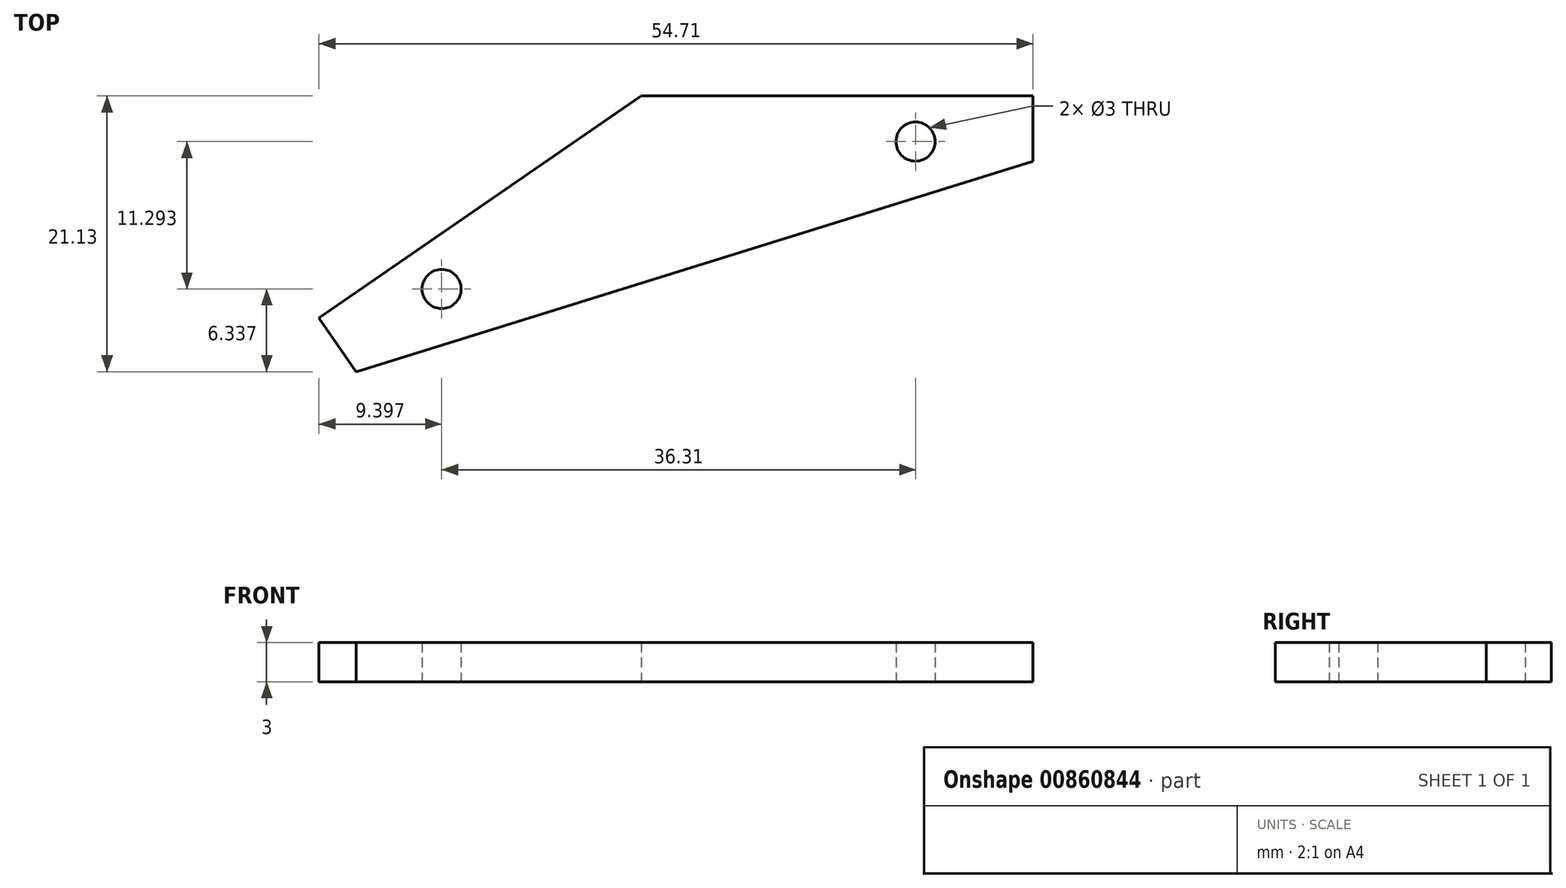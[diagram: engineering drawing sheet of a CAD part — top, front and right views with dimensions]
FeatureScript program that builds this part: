
annotation { "Feature Type Name" : "Feature", "Feature Type Description" : "" }
export const myFeature = defineFeature(function(context is Context, id is Id, definition is map)
    precondition{}
    {
        {
            var Q0;
            Q0=qCreatedBy(makeId("Top.planeOp"),FACE);
            var sketch = newSketch(context, id + "F0", { "sketchPlane" : qUnion([Q0])});
            skLineSegment(sketch, "E0", {"start": v(-50.25, 0) * mm, "end": v(-20.25, 0) * mm});
            skLineSegment(sketch, "E1", {"start": v(-50.25, 0) * mm, "end": v(-74.96, -17.02) * mm});
            skLineSegment(sketch, "E2", {"start": v(-74.96, -17.02) * mm, "end": v(-72.12, -21.13) * mm});
            skLineSegment(sketch, "E3", {"start": v(-72.12, -21.13) * mm, "end": v(-20.25, -5) * mm});
            skLineSegment(sketch, "E4", {"start": v(-20.25, -5) * mm, "end": v(-20.25, 0) * mm});
            skCircle(sketch, "E5", {"center": v(-65.56, -14.8) * mm, "radius": 1.5 * mm});
            skCircle(sketch, "E6", {"center": v(-29.25, -3.5) * mm, "radius": 1.5 * mm});
            skSolve(sketch);
        }
        {
            var Q0;
            Q0=makeQuery(id+"F0.imprint","IMPRINT",FACE,{"disambiguationData":[TD([[makeQuery(id+"F0.imprint","IMPRINT",EDGE,{"derivedFrom":sQuery(id+"F0.wireOp",EDGE,"E0")}),-1.0]])]});
            extrude(context, id + "F1", {"entities" : qUnion([Q0]), "depth" : 3 * mm, "offsetDistance" : 25 * mm});
        }
    });
